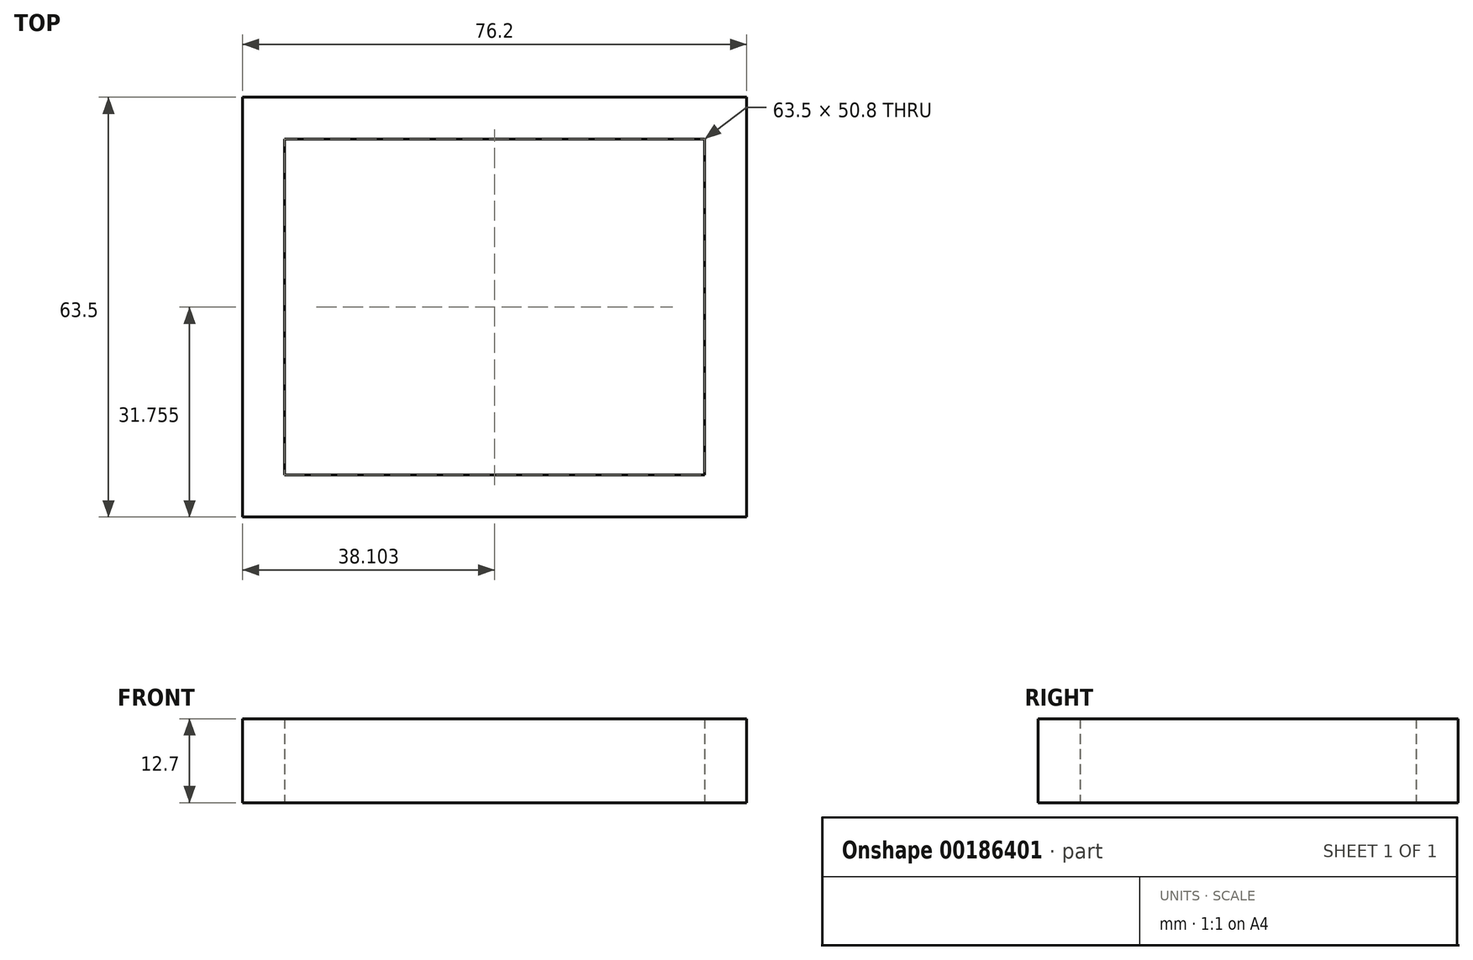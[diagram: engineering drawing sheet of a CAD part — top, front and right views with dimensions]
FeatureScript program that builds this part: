
annotation { "Feature Type Name" : "Feature", "Feature Type Description" : "" }
export const myFeature = defineFeature(function(context is Context, id is Id, definition is map)
    precondition{}
    {
        {
            var Q0;
            Q0=qCreatedBy(makeId("Top.planeOp"),FACE);
            var sketch = newSketch(context, id + "F0", { "sketchPlane" : qUnion([Q0])});
            skLineSegment(sketch, "E0.bottom", {"start": v(-82.23, 24.91) * mm, "end": v(-6.03, 24.91) * mm});
            skLineSegment(sketch, "E0.top", {"start": v(-82.23, -38.59) * mm, "end": v(-6.03, -38.59) * mm});
            skLineSegment(sketch, "E0.left", {"start": v(-82.23, 24.91) * mm, "end": v(-82.23, -38.59) * mm});
            skLineSegment(sketch, "E0.right", {"start": v(-6.03, 24.91) * mm, "end": v(-6.03, -38.59) * mm});
            skLineSegment(sketch, "E1.bottom", {"start": v(-75.88, 18.56) * mm, "end": v(-12.38, 18.56) * mm});
            skLineSegment(sketch, "E1.top", {"start": v(-75.88, -32.24) * mm, "end": v(-12.38, -32.24) * mm});
            skLineSegment(sketch, "E1.left", {"start": v(-75.88, 18.56) * mm, "end": v(-75.88, -32.24) * mm});
            skLineSegment(sketch, "E1.right", {"start": v(-12.38, 18.56) * mm, "end": v(-12.38, -32.24) * mm});
            skSolve(sketch);
        }
        {
            var Q0;
            Q0=makeQuery(id+"F0.imprint","IMPRINT",FACE,{"disambiguationData":[TD([[makeQuery(id+"F0.imprint","IMPRINT",EDGE,{"derivedFrom":sQuery(id+"F0.wireOp",EDGE,"E0.bottom")}),-1.0]])]});
            extrude(context, id + "F1", {"entities" : qUnion([Q0]), "depth" : 12.7 * mm});
        }
    });
